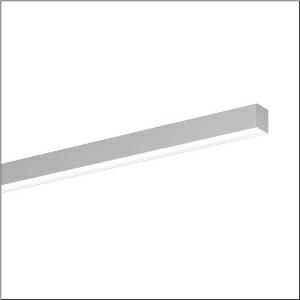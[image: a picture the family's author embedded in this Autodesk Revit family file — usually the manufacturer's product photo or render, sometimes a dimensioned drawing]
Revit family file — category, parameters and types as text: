
# Revit family: silica_21_51mx20tat2s
name_source: partatom
category: Lighting Fixtures
units: mm (PartAtom-declared; Revit-internal decimal feet)

## family parameters
Cut with Voids When Loaded = No
Host = Face
Light Source = No
Part Type = Normal
Room Calculation Point = No
Round Connector Dimension = Use Diameter
Shared = No

## types (1)
- --- (1 x LED, 2400 lm, 20.5 W, 6500K)
    Apparent Load = 21 VA
    CIE Flux Codes = 48 79 96 100 100
    Color Rendering = 80
    Color Temperature = 6500K
    Default Elevation = 1800 mm
    Description = Silica 21, office luminaire, primary optical cover: cover, of PMMA, opal, light emission: direct distribution, primary light characteristic: symmetric, installation type: surface-mounted, LED, rated luminous flux: 2.400lm, luminous efficacy: 112lm/W, light colour: 8tw, colour temperature: 2700..6500K, control gear: DALI DT8, with terminal, 3+2-pole, max. 2.5mm², mains connection: 220..240V, AC, 50/60Hz, rated input power: 21.5W, luminaire housing, of aluminium, metallic grey (RAL 9006), length: 1.204mm, width: 53mm, height: 53mm, protection rating (complete): IP20, insulation class (complete): insulation class I (protective earthing), certification: CE, permissible operating ambient temperature: 0..+35°C, standard: EN 50419, packaging unit: 1 piece
    Height = 53 mm
    Lamp = 1 x LED
    Lamp Light Flux = 2400 lm
    Lamp Power = 20.5 W
    Lamp count = 1
    Length = 1204 mm
    Luminous efficacy = 117 lm/W
    Manufacturer = Siteco
    ModVariant = No
    Model = 51MX20TAT2S
    Mounting Place = Ceiling
    Mounting Type = Surface mounted
    Number of Poles = 1
    OnlyDefault = Yes
    Power Factor = 1
    Product Name = Silica 21
    Product group = office luminaire | ceiling mounted
    ProductGroupID = 301
    Protection Class = Protection class I
    Protection Degree = IP 20
    RLX_Detail_Level = 1
    RLX_Emergency_Light_Flux = 0 lm
    RLX_Emergency_Type = 0
    RLX_Emergency_Type_DB = No
    RlxData = <blob elided: 23101 chars, md5=4bc19442>
    Socket = socket
    Standby Power = 0 W
    System Light Flux = 2400 lm
    System Power = 21 W
    Type Comments = individual setting
    Type Image = l_1335933.jpg
    URL = http://relux.com
    VarID = @adj_139169
    Voltage = 0 V
    Weight = 0.00 kg
    Width = 53 mm

## geometry (parser evidence)
native form markers: Blend x4, Sweep x11
no freeform markers — native parametric forms only
